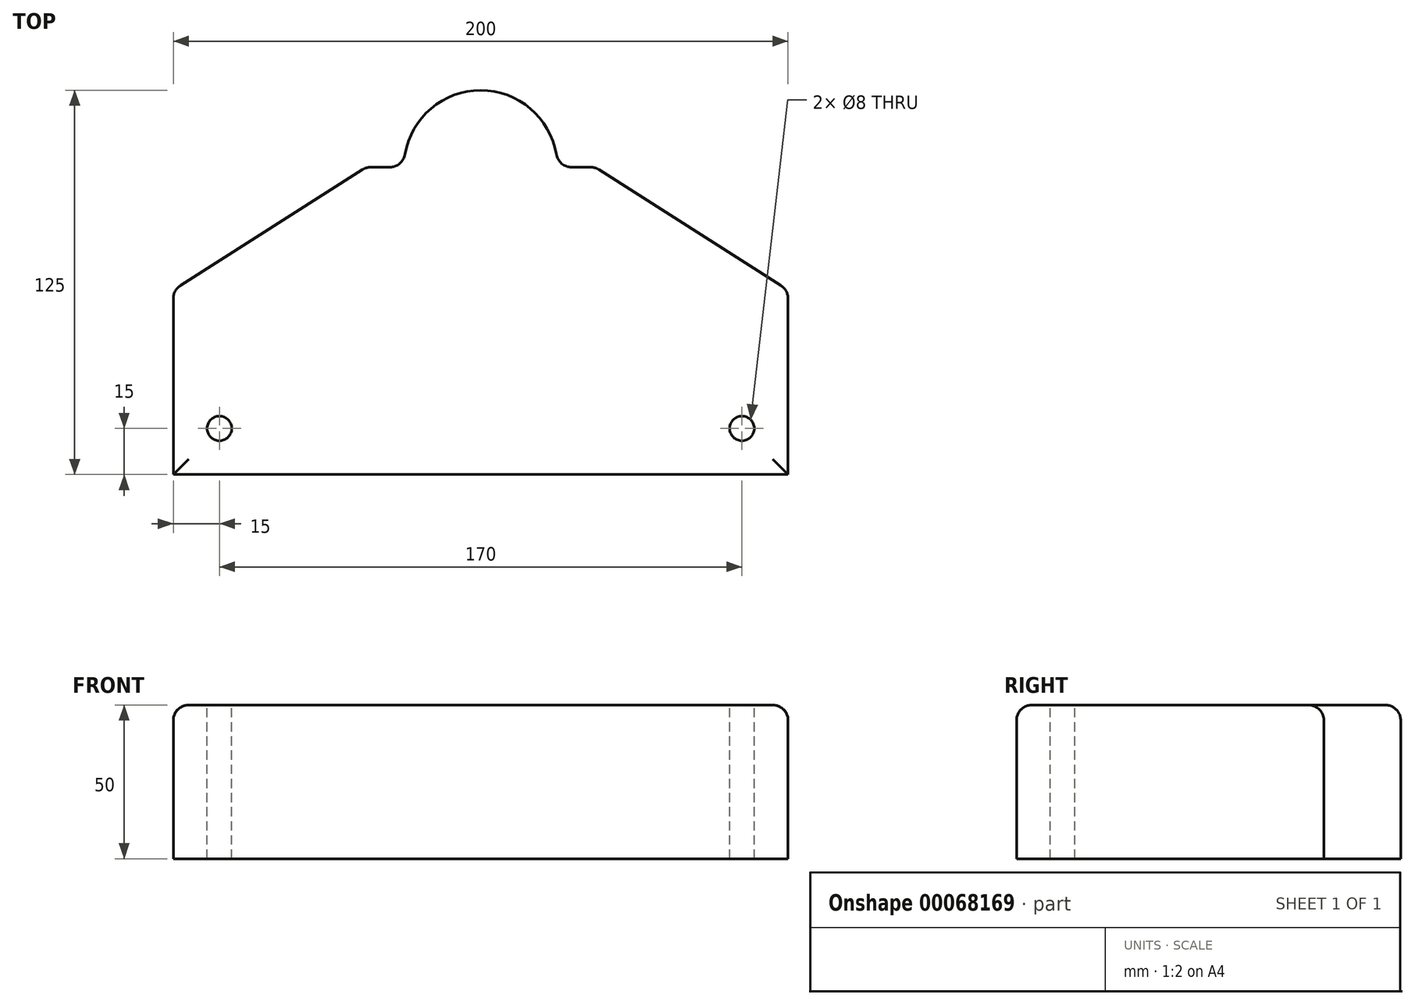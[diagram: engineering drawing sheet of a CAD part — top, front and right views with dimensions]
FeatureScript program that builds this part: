
annotation { "Feature Type Name" : "Feature", "Feature Type Description" : "" }
export const myFeature = defineFeature(function(context is Context, id is Id, definition is map)
    precondition{}
    {
        {
            var Q0;
            Q0=qCreatedBy(makeId("Top.planeOp"),FACE);
            var sketch = newSketch(context, id + "F0", { "sketchPlane" : qUnion([Q0])});
            skLineSegment(sketch, "E0", {"start": v(0, 0) * mm, "end": v(0, 57.26) * mm});
            skLineSegment(sketch, "E1", {"start": v(2.31, 61.47) * mm, "end": v(61.55, 99.22) * mm});
            skLineSegment(sketch, "E2", {"start": v(64.24, 100) * mm, "end": v(70.42, 100) * mm});
            skLineSegment(sketch, "E3", {"start": v(138.45, 99.22) * mm, "end": v(197.69, 61.47) * mm});
            skLineSegment(sketch, "E4", {"start": v(200, 57.26) * mm, "end": v(200, 0) * mm});
            skLineSegment(sketch, "E5", {"start": v(200, 0) * mm, "end": v(0, 0) * mm});
            skArc(sketch, "E6", {"start": v(124.65, 104.17) * mm, "mid": v(100, 125) * mm, "end": v(75.35, 104.17) * mm});
            skLineSegment(sketch, "E7.trimOffspring", {"start": v(129.58, 100) * mm, "end": v(135.76, 100) * mm});
            skPoint(sketch, "E8.visualSharp", {"position": v(75, 100) * mm});
            skArc(sketch, "E8.filletArc", {"start": v(70.42, 100) * mm, "mid": v(73.65, 101.18) * mm, "end": v(75.35, 104.17) * mm});
            skPoint(sketch, "E9.visualSharp", {"position": v(125, 100) * mm});
            skArc(sketch, "E9.filletArc", {"start": v(124.65, 104.17) * mm, "mid": v(126.35, 101.18) * mm, "end": v(129.58, 100) * mm});
            skPoint(sketch, "E10.visualSharp", {"position": v(137.22, 100) * mm});
            skArc(sketch, "E10.filletArc", {"start": v(138.45, 99.22) * mm, "mid": v(137.16, 99.8) * mm, "end": v(135.76, 100) * mm});
            skPoint(sketch, "E11.visualSharp", {"position": v(200, 60) * mm});
            skArc(sketch, "E11.filletArc", {"start": v(200, 57.26) * mm, "mid": v(199.38, 59.66) * mm, "end": v(197.69, 61.47) * mm});
            skPoint(sketch, "E12.visualSharp", {"position": v(62.78, 100) * mm});
            skArc(sketch, "E12.filletArc", {"start": v(64.24, 100) * mm, "mid": v(62.84, 99.8) * mm, "end": v(61.55, 99.22) * mm});
            skPoint(sketch, "E13.visualSharp", {"position": v(0, 60) * mm});
            skArc(sketch, "E13.filletArc", {"start": v(2.31, 61.47) * mm, "mid": v(0.62, 59.66) * mm, "end": v(0, 57.26) * mm});
            skSolve(sketch);
        }
        {
            var Q0;
            Q0=makeQuery(id+"F0.imprint","IMPRINT",FACE,{"disambiguationData":[TD([[makeQuery(id+"F0.imprint","IMPRINT",EDGE,{"derivedFrom":sQuery(id+"F0.wireOp",EDGE,"E0")}),-1.0]])]});
            extrude(context, id + "F1", {"entities" : qUnion([Q0]), "depth" : 50 * mm});
        }
        {
            var Q0;
            Q0=makeQuery(id+"F1.opExtrude","CAP_FACE",FACE,{"disambiguationData":[OSD([sQuery(id+"F0.wireOp",EDGE,"E0"),sQuery(id+"F0.wireOp",EDGE,"E1"),sQuery(id+"F0.wireOp",EDGE,"E2"),sQuery(id+"F0.wireOp",EDGE,"E3"),sQuery(id+"F0.wireOp",EDGE,"E4"),sQuery(id+"F0.wireOp",EDGE,"E5"),sQuery(id+"F0.wireOp",EDGE,"E6"),sQuery(id+"F0.wireOp",EDGE,"E7.trimOffspring"),sQuery(id+"F0.wireOp",EDGE,"E8.filletArc"),sQuery(id+"F0.wireOp",EDGE,"E9.filletArc"),sQuery(id+"F0.wireOp",EDGE,"E10.filletArc"),sQuery(id+"F0.wireOp",EDGE,"E11.filletArc"),sQuery(id+"F0.wireOp",EDGE,"E12.filletArc"),sQuery(id+"F0.wireOp",EDGE,"E13.filletArc")])],"isStart":false});
            fillet(context, id + "F2", {"entities" : qUnion([Q0]), "radius" : 5 * mm, "tangentPropagation" : true, "allowEdgeOverflow" : false});
        }
        {
            var Q0;
            Q0=makeQuery(id+"F1.opExtrude","CAP_FACE",FACE,{"disambiguationData":[OSD([sQuery(id+"F0.wireOp",EDGE,"E0"),sQuery(id+"F0.wireOp",EDGE,"E1"),sQuery(id+"F0.wireOp",EDGE,"E2"),sQuery(id+"F0.wireOp",EDGE,"E3"),sQuery(id+"F0.wireOp",EDGE,"E4"),sQuery(id+"F0.wireOp",EDGE,"E5"),sQuery(id+"F0.wireOp",EDGE,"E6"),sQuery(id+"F0.wireOp",EDGE,"E7.trimOffspring"),sQuery(id+"F0.wireOp",EDGE,"E8.filletArc"),sQuery(id+"F0.wireOp",EDGE,"E9.filletArc"),sQuery(id+"F0.wireOp",EDGE,"E10.filletArc"),sQuery(id+"F0.wireOp",EDGE,"E11.filletArc"),sQuery(id+"F0.wireOp",EDGE,"E12.filletArc"),sQuery(id+"F0.wireOp",EDGE,"E13.filletArc")])],"isStart":false});
            var sketch = newSketch(context, id + "F3", { "sketchPlane" : qUnion([Q0])});
            skCircle(sketch, "E14", {"center": v(15, 15) * mm, "radius": 4 * mm});
            skCircle(sketch, "E15", {"center": v(185, 15) * mm, "radius": 4 * mm});
            skSolve(sketch);
        }
        {
            var Q0;
            Q0=makeQuery(id+"F3.imprint","IMPRINT",FACE,{"disambiguationData":[TD([[makeQuery(id+"F3.imprint","IMPRINT",EDGE,{"derivedFrom":sQuery(id+"F3.wireOp",EDGE,"E15")}),1.0]])]});
            var Q1;
            Q1=makeQuery(id+"F3.imprint","IMPRINT",FACE,{"disambiguationData":[TD([[makeQuery(id+"F3.imprint","IMPRINT",EDGE,{"derivedFrom":sQuery(id+"F3.wireOp",EDGE,"E14")}),1.0]])]});
            extrude(context, id + "F4", {"entities" : qUnion([Q0, Q1]), "operationType" : NewBodyOperationType.REMOVE, "endBound" : BoundingType.THROUGH_ALL, "oppositeDirection" : true, "depth" : 25 * mm});
        }
    });
